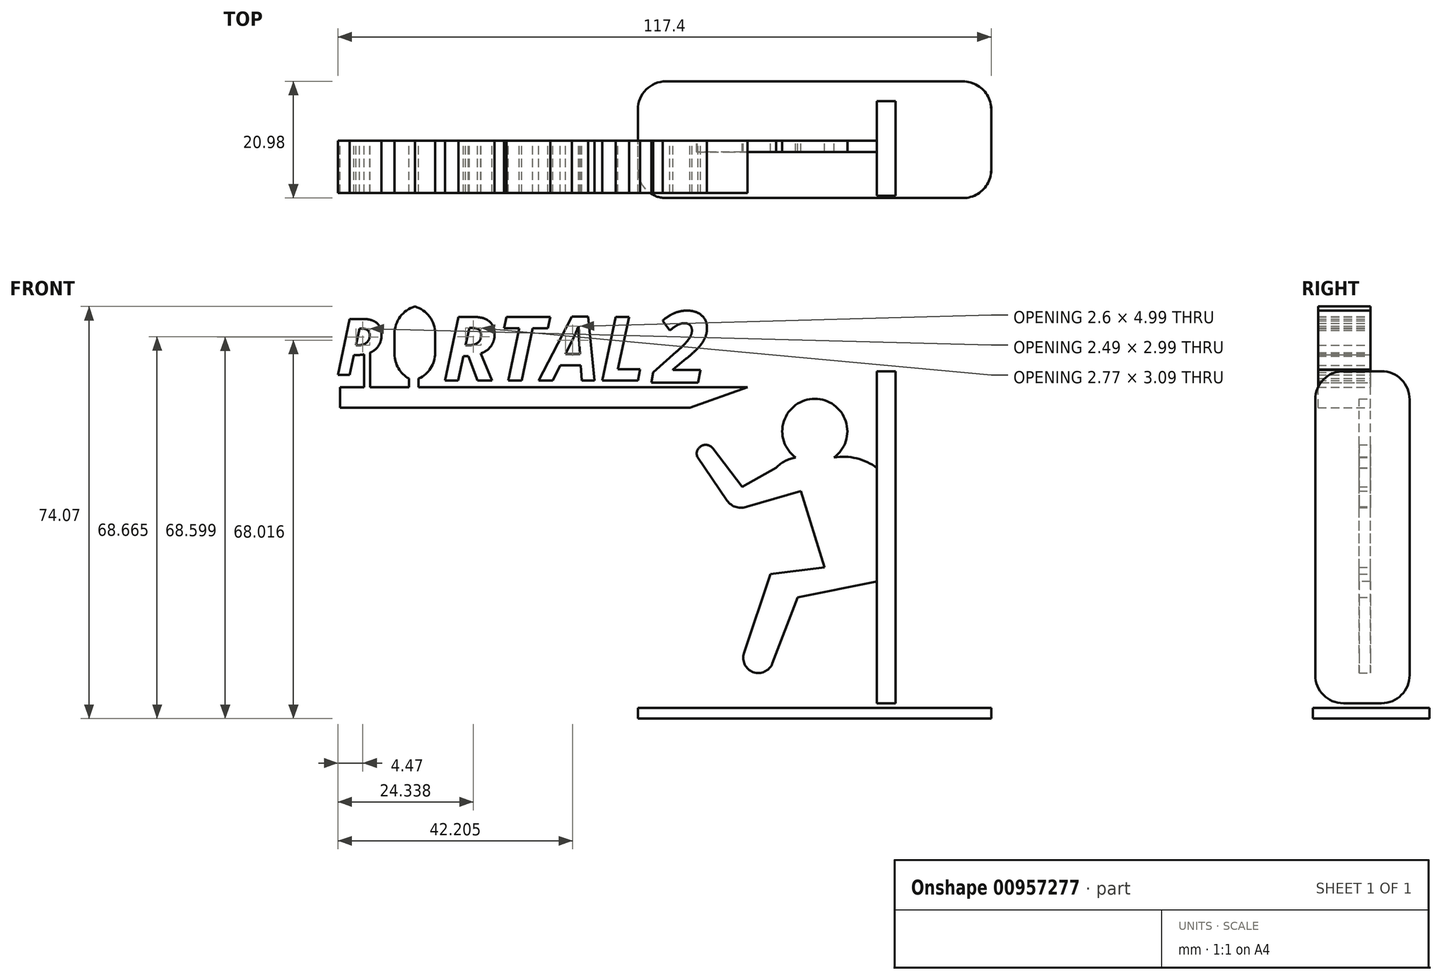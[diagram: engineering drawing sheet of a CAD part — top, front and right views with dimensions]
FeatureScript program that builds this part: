
annotation { "Feature Type Name" : "Feature", "Feature Type Description" : "" }
export const myFeature = defineFeature(function(context is Context, id is Id, definition is map)
    precondition{}
    {
        {
            var Q0;
            Q0=qCreatedBy(makeId("Front.planeOp"),FACE);
            var sketch = newSketch(context, id + "F0", { "sketchPlane" : qUnion([Q0])});
            skArc(sketch, "E0", {"start": v(12.31, 19.74) * mm, "mid": v(10.42, 19.12) * mm, "end": v(8.83, 17.92) * mm});
            skArc(sketch, "E1", {"start": v(19.22, 19.74) * mm, "mid": v(15.77, 30.3) * mm, "end": v(12.31, 19.74) * mm});
            skArc(sketch, "E2", {"start": v(27.04, 17.79) * mm, "mid": v(23.33, 19.58) * mm, "end": v(19.22, 19.74) * mm});
            skLineSegment(sketch, "E3", {"start": v(27.04, 17.79) * mm, "end": v(27.04, -2.54) * mm});
            skLineSegment(sketch, "E4", {"start": v(27.04, -2.54) * mm, "end": v(12.7, -5.4) * mm});
            skLineSegment(sketch, "E5", {"start": v(12.7, -5.4) * mm, "end": v(8.14, -17.27) * mm});
            skArc(sketch, "E6", {"start": v(3.06, -15.44) * mm, "mid": v(4.71, -18.84) * mm, "end": v(8.14, -17.27) * mm});
            skLineSegment(sketch, "E7", {"start": v(3.06, -15.44) * mm, "end": v(7.81, -1.21) * mm});
            skLineSegment(sketch, "E8", {"start": v(7.81, -1.21) * mm, "end": v(17.53, 0) * mm});
            skLineSegment(sketch, "E9", {"start": v(17.53, 0) * mm, "end": v(13.25, 13.7) * mm});
            skLineSegment(sketch, "E10", {"start": v(8.83, 17.92) * mm, "end": v(2.72, 14.5) * mm});
            skLineSegment(sketch, "E11", {"start": v(2.72, 14.5) * mm, "end": v(-2.56, 21.4) * mm});
            skArc(sketch, "E12", {"start": v(-2.56, 21.4) * mm, "mid": v(-4.6, 21.85) * mm, "end": v(-5.36, 19.9) * mm});
            skLineSegment(sketch, "E13", {"start": v(-5.36, 19.9) * mm, "end": v(0, 12.02) * mm});
            skArc(sketch, "E14", {"start": v(0, 12.02) * mm, "mid": v(1.63, 10.84) * mm, "end": v(3.64, 10.95) * mm});
            skLineSegment(sketch, "E15", {"start": v(3.64, 10.95) * mm, "end": v(13.25, 13.7) * mm});
            skSolve(sketch);
        }
        {
            var Q0;
            Q0 = qSketchRegion(id + "F0", true);
            extrude(context, id + "F1", {"entities" : qUnion([Q0]), "depth" : 2.03 * mm, "offsetDistance" : 25.4 * mm});
        }
        {
            var Q0;
            Q0=qCreatedBy(makeId("Front.planeOp"),FACE);
            var sketch = newSketch(context, id + "F2", { "sketchPlane" : qUnion([Q0])});
            skLineSegment(sketch, "E16", {"start": v(42.55, 29.65) * mm, "end": v(37.85, 29.65) * mm});
            skLineSegment(sketch, "E17", {"start": v(37.85, 29.65) * mm, "end": v(37.85, -14.4) * mm});
            skLineSegment(sketch, "E18", {"start": v(37.85, -14.4) * mm, "end": v(41.5, -14.4) * mm});
            skLineSegment(sketch, "E19", {"start": v(41.5, -14.4) * mm, "end": v(42.55, 29.65) * mm});
            skSolve(sketch);
        }
        {
            var Q0;
            Q0=qCreatedBy(makeId("Front.planeOp"),FACE);
            var sketch = newSketch(context, id + "F3", { "sketchPlane" : qUnion([Q0])});
            skLineSegment(sketch, "E20", {"start": v(37.85, 29.65) * mm, "end": v(42.54, 29.65) * mm});
            skLineSegment(sketch, "E21", {"start": v(42.54, 29.65) * mm, "end": v(41.5, -14.4) * mm});
            skLineSegment(sketch, "E22", {"start": v(41.5, -14.4) * mm, "end": v(37.86, -14.4) * mm});
            skLineSegment(sketch, "E23", {"start": v(37.86, -14.4) * mm, "end": v(37.85, 29.65) * mm});
            skSolve(sketch);
        }
        {
            var Q0;
            Q0=makeQuery(id+"F3.imprint","IMPRINT",FACE,{"disambiguationData":[TD([[makeQuery(id+"F3.imprint","IMPRINT",EDGE,{"derivedFrom":sQuery(id+"F3.wireOp",EDGE,"E20")}),-1.0]])]});
            extrude(context, id + "F4", {"entities" : qUnion([Q0]), "depth" : 11.94 * mm, "offsetDistance" : 25.4 * mm});
        }
        {
            var Q0;
            Q0=makeQuery(id+"F2.imprint","IMPRINT",FACE,{"disambiguationData":[TD([[makeQuery(id+"F2.imprint","IMPRINT",EDGE,{"derivedFrom":sQuery(id+"F2.wireOp",EDGE,"E16")}),1.0]])]});
            extrude(context, id + "F5", {"entities" : qUnion([Q0]), "operationType" : NewBodyOperationType.ADD, "oppositeDirection" : true, "depth" : 9.7 * mm, "offsetDistance" : 25.4 * mm});
        }
        {
            var Q0;
            Q0=makeQuery(id+"F4.opExtrude","SWEPT_FACE",FACE,{"disambiguationData":[OSD([sQuery(id+"F3.wireOp",EDGE,"E23")])]});
            extrude(context, id + "F6", {"entities" : qUnion([Q0]), "depth" : 12.14 * mm, "offsetDistance" : 25.4 * mm});
        }
        {
            var Q0;
            Q0=makeQuery(id+"F5.opExtrude","SWEPT_FACE",FACE,{"disambiguationData":[OSD([sQuery(id+"F2.wireOp",EDGE,"E17")])]});
            extrude(context, id + "F7", {"entities" : qUnion([Q0]), "depth" : 12.2 * mm, "offsetDistance" : 25.4 * mm});
        }
        {
            var Q0;
            Q0=makeQuery(id+"F4.opExtrude","SWEPT_BODY",BODY,{"disambiguationData":[OSD([sQuery(id+"F3.wireOp",EDGE,"E20"),sQuery(id+"F3.wireOp",EDGE,"E21"),sQuery(id+"F3.wireOp",EDGE,"E22"),sQuery(id+"F3.wireOp",EDGE,"E23")])]});
            deleteBodies(context, id + "F8", {"entities" : qUnion([Q0])});
        }
        {
            var Q0;
            Q0=makeQuery(id+"F7.opExtrude","CAP_FACE",FACE,{"disambiguationData":[OSD([sQuery(id+"F2.wireOp",EDGE,"E17")])],"isStart":true});
            extrude(context, id + "F9", {"entities" : qUnion([Q0]), "oppositeDirection" : true, "depth" : 11.2 * mm, "offsetDistance" : 25.4 * mm});
        }
        {
            var Q0;
            Q0=makeQuery(id+"F6.opExtrude","CAP_FACE",FACE,{"disambiguationData":[OSD([sQuery(id+"F3.wireOp",EDGE,"E23")])],"isStart":true});
            extrude(context, id + "F10", {"entities" : qUnion([Q0]), "oppositeDirection" : true, "depth" : 11.25 * mm, "offsetDistance" : 25.4 * mm});
        }
        {
            var Q0;
            Q0=makeQuery(id+"F6.opExtrude","SWEPT_BODY",BODY,{"disambiguationData":[OSD([sQuery(id+"F3.wireOp",EDGE,"E23")])]});
            deleteBodies(context, id + "F11", {"entities" : qUnion([Q0])});
        }
        {
            var Q0;
            Q0=makeQuery(id+"F7.opExtrude","SWEPT_BODY",BODY,{"disambiguationData":[OSD([sQuery(id+"F2.wireOp",EDGE,"E17")])]});
            deleteBodies(context, id + "F12", {"entities" : qUnion([Q0])});
        }
        {
            var Q0;
            Q0=makeQuery(id+"F9.opExtrude","CAP_FACE",FACE,{"disambiguationData":[OSD([sQuery(id+"F2.wireOp",EDGE,"E17")])],"isStart":true});
            extrude(context, id + "F13", {"entities" : qUnion([Q0]), "oppositeDirection" : true, "depth" : 10.08 * mm, "offsetDistance" : 25.4 * mm});
        }
        {
            var Q0;
            Q0=makeQuery(id+"F9.opExtrude","SWEPT_BODY",BODY,{"disambiguationData":[OSD([sQuery(id+"F2.wireOp",EDGE,"E17")])]});
            deleteBodies(context, id + "F14", {"entities" : qUnion([Q0])});
        }
        {
            var Q0;
            Q0=makeQuery(id+"F13.opExtrude","CAP_FACE",FACE,{"disambiguationData":[OSD([sQuery(id+"F2.wireOp",EDGE,"E17")])],"isStart":false});
            extrude(context, id + "F15", {"entities" : qUnion([Q0]), "depth" : 1.17 * mm, "offsetDistance" : 25.4 * mm});
        }
        {
            var Q0;
            Q0=makeQuery(id+"F10.opExtrude","SWEPT_BODY",BODY,{"disambiguationData":[OSD([sQuery(id+"F3.wireOp",EDGE,"E23")])]});
            deleteBodies(context, id + "F16", {"entities" : qUnion([Q0])});
        }
        {
            var Q0;
            Q0=makeQuery(id+"F13.opExtrude","SWEPT_BODY",BODY,{"disambiguationData":[OSD([sQuery(id+"F2.wireOp",EDGE,"E17")])]});
            deleteBodies(context, id + "F17", {"entities" : qUnion([Q0])});
        }
        {
            var Q0;
            Q0=makeQuery(id+"F15.opExtrude","SWEPT_BODY",BODY,{"disambiguationData":[OSD([sQuery(id+"F2.wireOp",EDGE,"E17")])]});
            deleteBodies(context, id + "F18", {"entities" : qUnion([Q0])});
        }
        {
            var Q0;
            Q0=qCreatedBy(makeId("Top.planeOp"),FACE);
            var sketch = newSketch(context, id + "F19", { "sketchPlane" : qUnion([Q0])});
            skLineSegment(sketch, "E24", {"start": v(27.21, 7.01) * mm, "end": v(27.21, -9.92) * mm});
            skLineSegment(sketch, "E25", {"start": v(27.21, -9.92) * mm, "end": v(27.5, -9.92) * mm});
            skLineSegment(sketch, "E26", {"start": v(27.5, -9.92) * mm, "end": v(27.5, 7.05) * mm});
            skLineSegment(sketch, "E27", {"start": v(27.5, 7.05) * mm, "end": v(27.21, 7.05) * mm});
            skLineSegment(sketch, "E28", {"start": v(27.21, 7.05) * mm, "end": v(27.21, 7.01) * mm});
            skSolve(sketch);
        }
        {
            var Q0;
            Q0 = qSketchRegion(id + "F19", true);
            extrude(context, id + "F20", {"entities" : qUnion([Q0]), "depth" : 35.26 * mm, "offsetDistance" : 25.4 * mm});
        }
        {
            var Q0;
            Q0=makeQuery(id+"F20.opExtrude","CAP_FACE",FACE,{"disambiguationData":[OSD([sQuery(id+"F19.wireOp",EDGE,"E24"),sQuery(id+"F19.wireOp",EDGE,"E25"),sQuery(id+"F19.wireOp",EDGE,"E26"),sQuery(id+"F19.wireOp",EDGE,"SanbzYMj-QkWq-I2x0-i9lF-L1NSehKOPGd9")])],"isStart":true});
            extrude(context, id + "F21", {"entities" : qUnion([Q0]), "operationType" : NewBodyOperationType.ADD, "depth" : 24.43 * mm, "offsetDistance" : 25.4 * mm});
        }
        {
            var Q0;
            {var subQ0=sQuery(id+"F19.wireOp",EDGE,"E24");Q0=makeQuery(id+"F21.boolean.opBoolean","MERGE",FACE,{"derivedFrom":[makeQuery(id+"F20.opExtrude","SWEPT_FACE",FACE,{"disambiguationData":[OSD([subQ0])]}),makeQuery(id+"F21.opExtrude","SWEPT_FACE",FACE,{"disambiguationData":[OSD([subQ0])]})]});}
            extrude(context, id + "F22", {"entities" : qUnion([Q0]), "operationType" : NewBodyOperationType.ADD, "depth" : 0.29 * mm, "offsetDistance" : 25.4 * mm});
        }
        {
            var Q0;
            {var subQ0=sQuery(id+"F19.wireOp",EDGE,"E25");var subQ1=sQuery(id+"F19.wireOp",EDGE,"E24");Q0=makeQuery(id+"F22.boolean.opBoolean","MERGE",EDGE,{"derivedFrom":[makeQuery(id+"F21.opExtrude","CAP_EDGE",EDGE,{"disambiguationData":[OSD([subQ0])],"isStart":false}),makeQuery(id+"F22.opExtrude","SWEPT_EDGE",EDGE,{"disambiguationData":[OSD([subQ1,subQ0]),TDD([makeQuery(id+"F21.opExtrude","CAP_VERTEX",VERTEX,{"disambiguationData":[OSD([subQ1,subQ0])],"isStart":false})])]})]});}
            fillet(context, id + "F23", {"entities" : qUnion([Q0]), "radius" : 5.08 * mm, "tangentPropagation" : true, "allowEdgeOverflow" : false});
        }
        {
            var Q0;
            Q0=makeQuery(id+"F22.opExtrude","SWEPT_FACE",FACE,{"disambiguationData":[OSD([sQuery(id+"F19.wireOp",EDGE,"E24"),sQuery(id+"F19.wireOp",EDGE,"E28")])]});
            extrude(context, id + "F24", {"entities" : qUnion([Q0]), "operationType" : NewBodyOperationType.ADD, "depth" : 0.04 * mm, "offsetDistance" : 25.4 * mm});
        }
        {
            var Q0;
            {var subQ0=sQuery(id+"F19.wireOp",EDGE,"E28");var subQ1=sQuery(id+"F19.wireOp",EDGE,"E24");Q0=makeQuery(id+"F24.opExtrude","CAP_EDGE",EDGE,{"disambiguationData":[OSD([subQ1,subQ0]),TDD([makeQuery(id+"F22.opExtrude","SWEPT_EDGE",EDGE,{"disambiguationData":[OSD([subQ1,subQ0]),TDD([makeQuery(id+"F21.opExtrude","CAP_VERTEX",VERTEX,{"disambiguationData":[OSD([subQ1,subQ0])],"isStart":false})])]})])],"isStart":false});}
            var Q1;
            Q1=makeQuery(id+"F20.opExtrude","CAP_EDGE",EDGE,{"disambiguationData":[OSD([sQuery(id+"F19.wireOp",EDGE,"E27")])],"isStart":false});
            var Q2;
            {var subQ0=sQuery(id+"F19.wireOp",EDGE,"E25");var subQ1=sQuery(id+"F19.wireOp",EDGE,"E24");Q2=makeQuery(id+"F22.boolean.opBoolean","MERGE",EDGE,{"derivedFrom":[makeQuery(id+"F20.opExtrude","CAP_EDGE",EDGE,{"disambiguationData":[OSD([subQ0])],"isStart":false}),makeQuery(id+"F22.opExtrude","SWEPT_EDGE",EDGE,{"disambiguationData":[OSD([subQ1,subQ0]),TDD([makeQuery(id+"F20.opExtrude","CAP_VERTEX",VERTEX,{"disambiguationData":[OSD([subQ1,subQ0])],"isStart":false})])]})]});}
            fillet(context, id + "F25", {"entities" : qUnion([Q0, Q1, Q2]), "radius" : 5.08 * mm, "tangentPropagation" : true, "allowEdgeOverflow" : false});
        }
        {
            var Q0;
            {var subQ0=sQuery(id+"F19.wireOp",EDGE,"E26");Q0=makeQuery(id+"F21.boolean.opBoolean","MERGE",FACE,{"derivedFrom":[makeQuery(id+"F20.opExtrude","SWEPT_FACE",FACE,{"disambiguationData":[OSD([subQ0])]}),makeQuery(id+"F21.opExtrude","SWEPT_FACE",FACE,{"disambiguationData":[OSD([subQ0])]})]});}
            extrude(context, id + "F26", {"entities" : qUnion([Q0]), "operationType" : NewBodyOperationType.ADD, "depth" : 2.8 * mm, "offsetDistance" : 25.4 * mm});
        }
        {
            var Q0;
            Q0=qCreatedBy(makeId("Front.planeOp"),FACE);
            var sketch = newSketch(context, id + "F27", { "sketchPlane" : qUnion([Q0])});
            skLineSegment(sketch, "E29", {"start": v(47.47, -25.24) * mm, "end": v(-16.03, -25.24) * mm});
            skLineSegment(sketch, "E30", {"start": v(-16.03, -25.24) * mm, "end": v(-16.03, -27.17) * mm});
            skLineSegment(sketch, "E31", {"start": v(-16.03, -27.17) * mm, "end": v(47.47, -27.17) * mm});
            skLineSegment(sketch, "E32", {"start": v(47.47, -27.17) * mm, "end": v(47.47, -25.24) * mm});
            skSolve(sketch);
        }
        {
            var Q0;
            Q0 = qSketchRegion(id + "F27", true);
            extrude(context, id + "F28", {"entities" : qUnion([Q0]), "depth" : 10.34 * mm, "offsetDistance" : 25.4 * mm});
        }
        {
            var Q0;
            Q0=makeQuery(id+"F28.opExtrude","CAP_FACE",FACE,{"disambiguationData":[OSD([sQuery(id+"F27.wireOp",EDGE,"E29"),sQuery(id+"F27.wireOp",EDGE,"E30"),sQuery(id+"F27.wireOp",EDGE,"E31"),sQuery(id+"F27.wireOp",EDGE,"E32")])],"isStart":true});
            extrude(context, id + "F29", {"entities" : qUnion([Q0]), "operationType" : NewBodyOperationType.ADD, "depth" : 10.64 * mm, "offsetDistance" : 25.4 * mm});
        }
        {
            var Q0;
            Q0=makeQuery(id+"F28.opExtrude","CAP_EDGE",EDGE,{"disambiguationData":[OSD([sQuery(id+"F27.wireOp",EDGE,"E30")])],"isStart":false});
            var Q1;
            Q1=makeQuery(id+"F29.opExtrude","CAP_EDGE",EDGE,{"disambiguationData":[OSD([sQuery(id+"F27.wireOp",EDGE,"E30")])],"isStart":false});
            var Q2;
            Q2=makeQuery(id+"F28.opExtrude","CAP_EDGE",EDGE,{"disambiguationData":[OSD([sQuery(id+"F27.wireOp",EDGE,"E32")])],"isStart":false});
            var Q3;
            Q3=makeQuery(id+"F29.opExtrude","CAP_EDGE",EDGE,{"disambiguationData":[OSD([sQuery(id+"F27.wireOp",EDGE,"E32")])],"isStart":false});
            fillet(context, id + "F30", {"entities" : qUnion([Q0, Q1, Q2, Q3]), "radius" : 5.08 * mm, "tangentPropagation" : true, "allowEdgeOverflow" : false});
        }
        {
            var Q0;
            Q0=qCreatedBy(makeId("Front.planeOp"),FACE);
            var sketch = newSketch(context, id + "F31", { "sketchPlane" : qUnion([Q0])});
            skLineSegment(sketch, "E33", {"start": v(-28.08, 28.73) * mm, "end": v(-69.52, 28.73) * mm});
            skLineSegment(sketch, "E34", {"start": v(-69.52, 28.73) * mm, "end": v(-69.52, 32.38) * mm});
            skLineSegment(sketch, "E35", {"start": v(-69.52, 32.38) * mm, "end": v(-28.08, 32.38) * mm});
            skText(sketch, "E36", { "text": "P", "fontName": "OpenSans-BoldItalic.ttf"});
            skLineSegment(sketch, "E37.bottom", {"start": v(-59.75, 47.1) * mm, "end": v(-52.45, 47.1) * mm});
            skLineSegment(sketch, "E37.top", {"start": v(-59.75, 33.95) * mm, "end": v(-52.45, 33.95) * mm});
            skLineSegment(sketch, "E37.left", {"start": v(-59.75, 47.1) * mm, "end": v(-59.75, 33.95) * mm});
            skLineSegment(sketch, "E37.right", {"start": v(-52.45, 47.1) * mm, "end": v(-52.45, 33.95) * mm});
            skText(sketch, "E38", { "text": "RTAL", "fontName": "OpenSans-BoldItalic.ttf"});
            skLineSegment(sketch, "E39", {"start": v(-28.08, 32.38) * mm, "end": v(3.67, 32.38) * mm});
            skLineSegment(sketch, "E40", {"start": v(3.67, 32.38) * mm, "end": v(-6.66, 28.73) * mm});
            skLineSegment(sketch, "E41", {"start": v(-6.66, 28.73) * mm, "end": v(-28.08, 28.73) * mm});
            skText(sketch, "E42", { "text": "2", "fontName": "OpenSans-BoldItalic.ttf"});
            skLineSegment(sketch, "E43", {"start": v(-68.1, 34.6) * mm, "end": v(-68.1, 32.38) * mm});
            skLineSegment(sketch, "E44", {"start": v(-69.44, 34.6) * mm, "end": v(-69.44, 32.38) * mm});
            skLineSegment(sketch, "E45", {"start": v(-64.12, 32.38) * mm, "end": v(-64.12, 38.67) * mm});
            skLineSegment(sketch, "E46", {"start": v(-65.23, 32.38) * mm, "end": v(-65.23, 38.33) * mm});
            skLineSegment(sketch, "E47", {"start": v(-57.17, 33.95) * mm, "end": v(-57.17, 32.38) * mm});
            skLineSegment(sketch, "E48", {"start": v(-55.41, 33.95) * mm, "end": v(-55.41, 32.38) * mm});
            skLineSegment(sketch, "E49", {"start": v(-42.7, 33.6) * mm, "end": v(-42.7, 32.38) * mm});
            skLineSegment(sketch, "E50", {"start": v(-44.3, 33.6) * mm, "end": v(-44.3, 32.38) * mm});
            skLineSegment(sketch, "E51", {"start": v(-48.91, 32.38) * mm, "end": v(-48.91, 33.6) * mm});
            skLineSegment(sketch, "E52", {"start": v(-50.1, 33.6) * mm, "end": v(-50.1, 32.38) * mm});
            skLineSegment(sketch, "E53", {"start": v(-37.49, 33.6) * mm, "end": v(-37.49, 32.38) * mm});
            skLineSegment(sketch, "E54", {"start": v(-38.79, 32.38) * mm, "end": v(-38.79, 33.6) * mm});
            skLineSegment(sketch, "E55", {"start": v(-32.17, 33.6) * mm, "end": v(-32.17, 32.38) * mm});
            skLineSegment(sketch, "E56", {"start": v(-33.2, 32.38) * mm, "end": v(-33.2, 33.6) * mm});
            skLineSegment(sketch, "E57", {"start": v(-24.16, 32.38) * mm, "end": v(-24.16, 33.6) * mm});
            skLineSegment(sketch, "E58", {"start": v(-25.67, 32.38) * mm, "end": v(-25.67, 33.6) * mm});
            skLineSegment(sketch, "E59", {"start": v(-16.3, 32.38) * mm, "end": v(-16.3, 33.6) * mm});
            skLineSegment(sketch, "E60", {"start": v(-17.75, 32.38) * mm, "end": v(-17.75, 33.6) * mm});
            skLineSegment(sketch, "E61", {"start": v(-20.25, 32.38) * mm, "end": v(-20.25, 33.6) * mm});
            skLineSegment(sketch, "E62", {"start": v(-21.46, 32.38) * mm, "end": v(-21.46, 33.6) * mm});
            skLineSegment(sketch, "E63", {"start": v(-5.9, 32.38) * mm, "end": v(-5.9, 33.2) * mm});
            skLineSegment(sketch, "E64", {"start": v(-6.51, 32.38) * mm, "end": v(-6.51, 33.2) * mm});
            skLineSegment(sketch, "E65", {"start": v(-9.27, 32.38) * mm, "end": v(-9.27, 33.2) * mm});
            skLineSegment(sketch, "E66", {"start": v(-10.38, 32.38) * mm, "end": v(-10.38, 33.2) * mm});
            const initialGuessF31  = {"E36": [-0.0703, 0.0346, 1, 0, 0.01016], "E38": [-0.05112, 0.0336, 1, 0, 0.01152], "E42": [-0.0132, 0.0332, 1, 0, 0.01289]};
            skSetInitialGuess(sketch, initialGuessF31);
            skSolve(sketch);
        }
        {
            var Q0;
            Q0 = qSketchRegion(id + "F31", true);
            extrude(context, id + "F32", {"entities" : qUnion([Q0]), "depth" : 9.4 * mm, "offsetDistance" : 25.4 * mm});
        }
        {
            var Q0;
            Q0 = qSketchRegion(id + "F31", true);
            extrude(context, id + "F33", {"entities" : qUnion([Q0]), "operationType" : NewBodyOperationType.ADD, "depth" : 6.1 * mm, "offsetDistance" : 25.4 * mm});
        }
        {
            var Q0;
            Q0=makeQuery(id+"F32.opExtrude","SWEPT_EDGE",EDGE,{"disambiguationData":[OSD([sQuery(id+"F31.wireOp",EDGE,"E37.top"),sQuery(id+"F31.wireOp",EDGE,"E37.right")])]});
            var Q1;
            Q1=makeQuery(id+"F32.opExtrude","SWEPT_EDGE",EDGE,{"disambiguationData":[OSD([sQuery(id+"F31.wireOp",EDGE,"E37.top"),sQuery(id+"F31.wireOp",EDGE,"E37.left")])]});
            var Q2;
            Q2=makeQuery(id+"F32.opExtrude","SWEPT_EDGE",EDGE,{"disambiguationData":[OSD([sQuery(id+"F31.wireOp",EDGE,"E37.bottom"),sQuery(id+"F31.wireOp",EDGE,"E37.right")])]});
            var Q3;
            Q3=makeQuery(id+"F32.opExtrude","SWEPT_EDGE",EDGE,{"disambiguationData":[OSD([sQuery(id+"F31.wireOp",EDGE,"E37.bottom"),sQuery(id+"F31.wireOp",EDGE,"E37.left")])]});
            fillet(context, id + "F34", {"entities" : qUnion([Q0, Q1, Q2, Q3]), "radius" : 5.08 * mm, "tangentPropagation" : true, "allowEdgeOverflow" : false});
        }
        {
            var Q0;
            Q0=qCreatedBy(makeId("Right.planeOp"),FACE);
            var sketch = newSketch(context, id + "F35", { "sketchPlane" : qUnion([Q0])});
            skLineSegment(sketch, "E67.bottom", {"start": v(177.8, 61.13) * mm, "end": v(152.4, 61.13) * mm});
            skLineSegment(sketch, "E67.top", {"start": v(177.8, -35.26) * mm, "end": v(152.4, -35.26) * mm});
            skLineSegment(sketch, "E67.left", {"start": v(177.8, 61.13) * mm, "end": v(177.8, -35.26) * mm});
            skLineSegment(sketch, "E67.right", {"start": v(152.4, 61.13) * mm, "end": v(152.4, -35.26) * mm});
            skLineSegment(sketch, "E68.top", {"start": v(177.8, -28.9) * mm, "end": v(152.4, -28.9) * mm});
            skLineSegment(sketch, "E68.left", {"start": v(177.8, -35.26) * mm, "end": v(177.8, -28.9) * mm});
            skLineSegment(sketch, "E68.right", {"start": v(152.4, -35.26) * mm, "end": v(152.4, -28.9) * mm});
            skSolve(sketch);
        }
        {
            var Q0;
            {var subQ0=sQuery(id+"F35.wireOp",EDGE,"E67.top");Q0=makeQuery(id+"F35.imprint","IMPRINT",FACE,{"disambiguationData":[TD([[makeQuery(id+"F35.imprint","IMPRINT",EDGE,{"derivedFrom":subQ0}),-1.0]])]});}
            extrude(context, id + "F36", {"entities" : qUnion([Q0]), "depth" : 50.8 * mm, "offsetDistance" : 25.4 * mm});
        }
        {
            var Q0;
            {var subQ0=sQuery(id+"F35.wireOp",EDGE,"E67.bottom");Q0=makeQuery(id+"F35.imprint","IMPRINT",FACE,{"disambiguationData":[TD([[makeQuery(id+"F35.imprint","IMPRINT",EDGE,{"derivedFrom":subQ0}),1.0]])]});}
            extrude(context, id + "F37", {"entities" : qUnion([Q0]), "operationType" : NewBodyOperationType.ADD, "depth" : 5.08 * mm, "offsetDistance" : 25.4 * mm});
        }
        {
            var Q0;
            Q0=qCreatedBy(makeId("Front.planeOp"),FACE);
            cPlane(context, id + "F38", {"entities" : qUnion([Q0]), "cplaneType" : CPlaneType.OFFSET, "offset" : 161.8 * mm, "oppositeDirection" : true, "width" : 152.4 * mm, "height" : 152.4 * mm});
        }
        {
            var Q0;
            Q0=makeQuery(id+"F36.opExtrude","SWEPT_BODY",BODY,{"disambiguationData":[OSD([sQuery(id+"F35.wireOp",EDGE,"E67.top"),sQuery(id+"F35.wireOp",EDGE,"E67.left"),sQuery(id+"F35.wireOp",EDGE,"E67.right"),sQuery(id+"F35.wireOp",EDGE,"E68.top")])]});
            deleteBodies(context, id + "F39", {"entities" : qUnion([Q0])});
        }
    });
